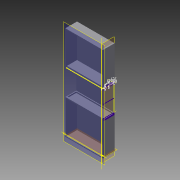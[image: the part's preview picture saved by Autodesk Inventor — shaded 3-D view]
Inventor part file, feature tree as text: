
AUTODESK INVENTOR PART (.ipt)
format: ipt  version: 2015 (Build 190159000, 159)  size: 167,424 bytes
history: native  units: mm
features: sketch x9, extrude x5, projected_geometry x3
ambient origin geometry x8: Origin, YZ Plane, XZ Plane, XY Plane, X Axis, Y Axis, Z Axis, Center Point
bodies: Solid1 (feature_tree)
feature tree (17):
  sketch  "Sketch1"  dims[d0=241.25mm d1=96.5mm]
  sketch  "Sketch2"  dims[d2=30.0mm d3=0.0mm d4=64.0mm]
  extrude  "Extrusion1"  Depth=96.5mm
  extrude  "Extrusion2"  Depth=64.0mm
  extrude  "Extrusion3"  Depth=96.5mm
  sketch  "Sketch6"  dims[d12=28.0mm d13=0.0mm]
  sketch  "Sketch7"  dims[d28=2.0mm]
  sketch  "Sketch9"  dims[d29=4.0mm]
  extrude  "Extrusion5"  Depth=28.0mm TaperAngle=0.0deg
  extrude  "Extrusion6"  Depth=2.0mm
  sketch  "Sketch11"  dims[d30=3.0mm d31=2.0mm d32=2.0mm d33=0.0mm d34=94.5mm d35=0.0mm d36=22.0mm d37=2.0mm d38=5.0mm]
  sketch  "Sketch3"  dims[d5=0.0mm d6=96.5mm]
  sketch  "Sketch4"  dims[d7=0.0mm d8=28.0mm d9=0.0mm]
  sketch  "Sketch5"  dims[d10=2.0mm d11=2.0mm]
  projected_geometry  "Projected Loop1"
  projected_geometry  "Projected Loop2"
  projected_geometry  "Projected Loop3"
